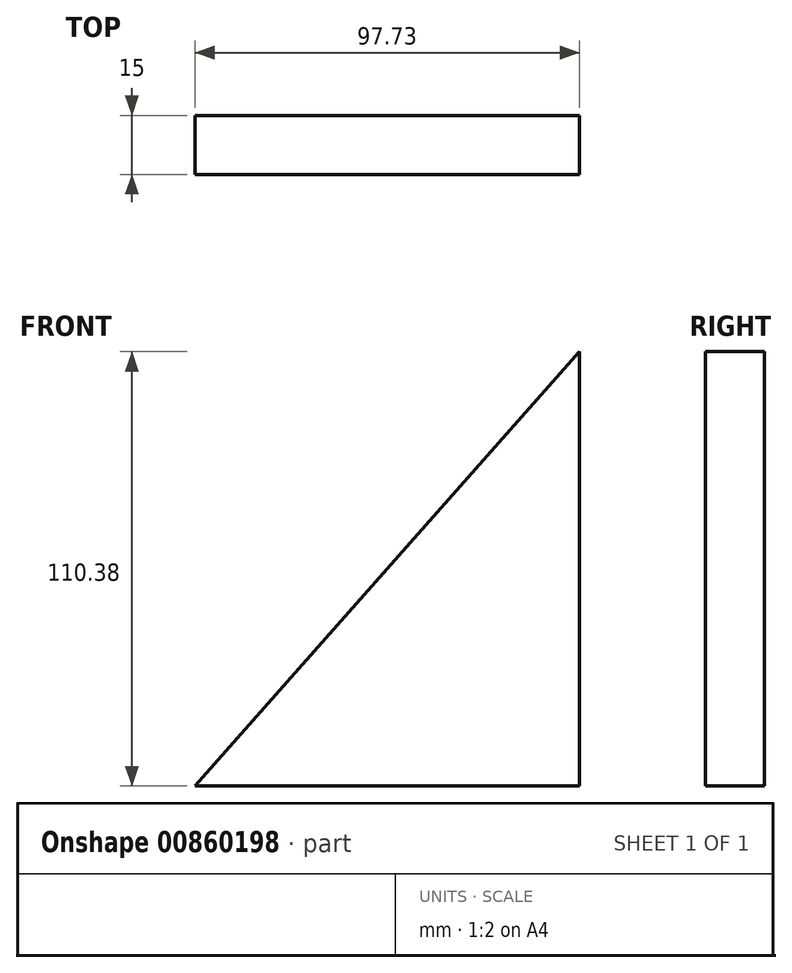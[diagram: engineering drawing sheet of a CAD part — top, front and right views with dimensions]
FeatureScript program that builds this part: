
annotation { "Feature Type Name" : "Feature", "Feature Type Description" : "" }
export const myFeature = defineFeature(function(context is Context, id is Id, definition is map)
    precondition{}
    {
        {
            var Q0;
            Q0=qCreatedBy(makeId("Front.planeOp"),FACE);
            var sketch = newSketch(context, id + "F0", { "sketchPlane" : qUnion([Q0])});
            skLineSegment(sketch, "E0", {"start": v(-47.75, -53.17) * mm, "end": v(49.98, 57.2) * mm});
            skLineSegment(sketch, "E1", {"start": v(49.98, 57.2) * mm, "end": v(49.98, -53.17) * mm});
            skLineSegment(sketch, "E2", {"start": v(49.98, -53.17) * mm, "end": v(-47.75, -53.17) * mm});
            skSolve(sketch);
        }
        {
            var Q0;
            Q0=makeQuery(id+"F0.imprint","IMPRINT",FACE,{"disambiguationData":[TD([[makeQuery(id+"F0.imprint","IMPRINT",EDGE,{"derivedFrom":sQuery(id+"F0.wireOp",EDGE,"E0")}),-1.0]])]});
            extrude(context, id + "F1", {"entities" : qUnion([Q0]), "depth" : 15 * mm, "offsetDistance" : 25 * mm});
        }
    });
